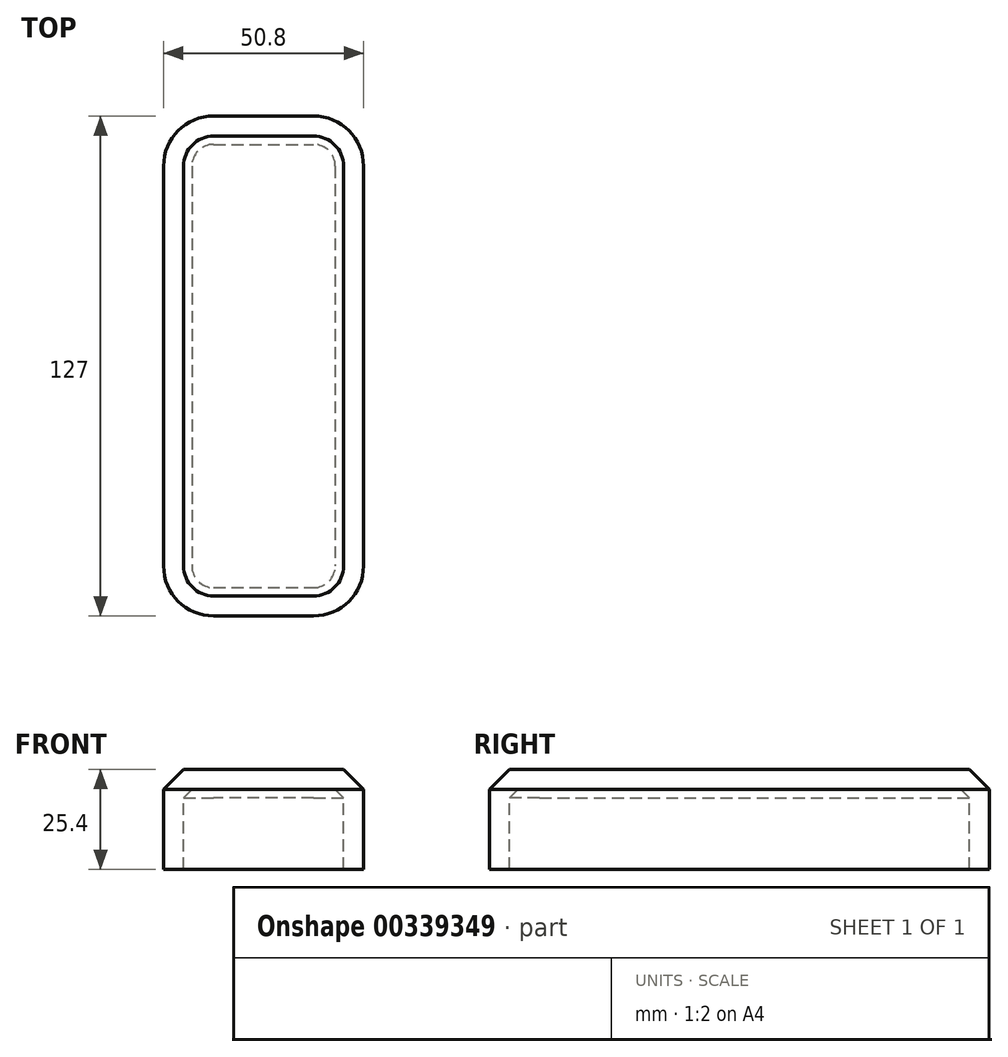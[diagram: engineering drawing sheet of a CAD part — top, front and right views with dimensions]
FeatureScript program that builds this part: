
annotation { "Feature Type Name" : "Feature", "Feature Type Description" : "" }
export const myFeature = defineFeature(function(context is Context, id is Id, definition is map)
    precondition{}
    {
        {
            var Q0;
            Q0=qCreatedBy(makeId("Front.planeOp"),FACE);
            var sketch = newSketch(context, id + "F0", { "sketchPlane" : qUnion([Q0])});
            skLineSegment(sketch, "E0.bottom", {"start": v(0, 25.4) * mm, "end": v(50.8, 25.4) * mm});
            skLineSegment(sketch, "E0.top", {"start": v(0, 0) * mm, "end": v(50.8, 0) * mm});
            skLineSegment(sketch, "E0.left", {"start": v(0, 25.4) * mm, "end": v(0, 0) * mm});
            skLineSegment(sketch, "E0.right", {"start": v(50.8, 25.4) * mm, "end": v(50.8, 0) * mm});
            skSolve(sketch);
        }
        {
            var Q0;
            Q0 = qSketchRegion(id + "F0", true);
            extrude(context, id + "F1", {"entities" : qUnion([Q0]), "depth" : -127 * mm});
        }
        {
            var Q0;
            Q0=makeQuery(id+"F1.opExtrude","CAP_EDGE",EDGE,{"disambiguationData":[OSD([sQuery(id+"F0.wireOp",EDGE,"E0.left")])],"isStart":true});
            var Q1;
            Q1=makeQuery(id+"F1.opExtrude","CAP_EDGE",EDGE,{"disambiguationData":[OSD([sQuery(id+"F0.wireOp",EDGE,"E0.right")])],"isStart":true});
            var Q2;
            Q2=makeQuery(id+"F1.opExtrude","CAP_EDGE",EDGE,{"disambiguationData":[OSD([sQuery(id+"F0.wireOp",EDGE,"E0.right")])],"isStart":false});
            var Q3;
            Q3=makeQuery(id+"F1.opExtrude","CAP_EDGE",EDGE,{"disambiguationData":[OSD([sQuery(id+"F0.wireOp",EDGE,"E0.left")])],"isStart":false});
            fillet(context, id + "F2", {"entities" : qUnion([Q0, Q1, Q2, Q3]), "radius" : 12.7 * mm, "tangentPropagation" : true, "allowEdgeOverflow" : false});
        }
        {
            var Q0;
            Q0=makeQuery(id+"F1.opExtrude","SWEPT_EDGE",EDGE,{"disambiguationData":[OSD([sQuery(id+"F0.wireOp",EDGE,"E0.bottom"),sQuery(id+"F0.wireOp",EDGE,"E0.right")])]});
            chamfer(context, id + "F3", {"entities" : qUnion([Q0]), "width" : 5.08 * mm, "tangentPropagation" : true});
        }
        {
            var Q0;
            Q0=makeQuery(id+"F1.opExtrude","SWEPT_FACE",FACE,{"disambiguationData":[OSD([sQuery(id+"F0.wireOp",EDGE,"E0.top")])]});
            shell(context, id + "F4", {"entities" : qUnion([Q0]), "thickness" : 5.08 * mm});
        }
    });
